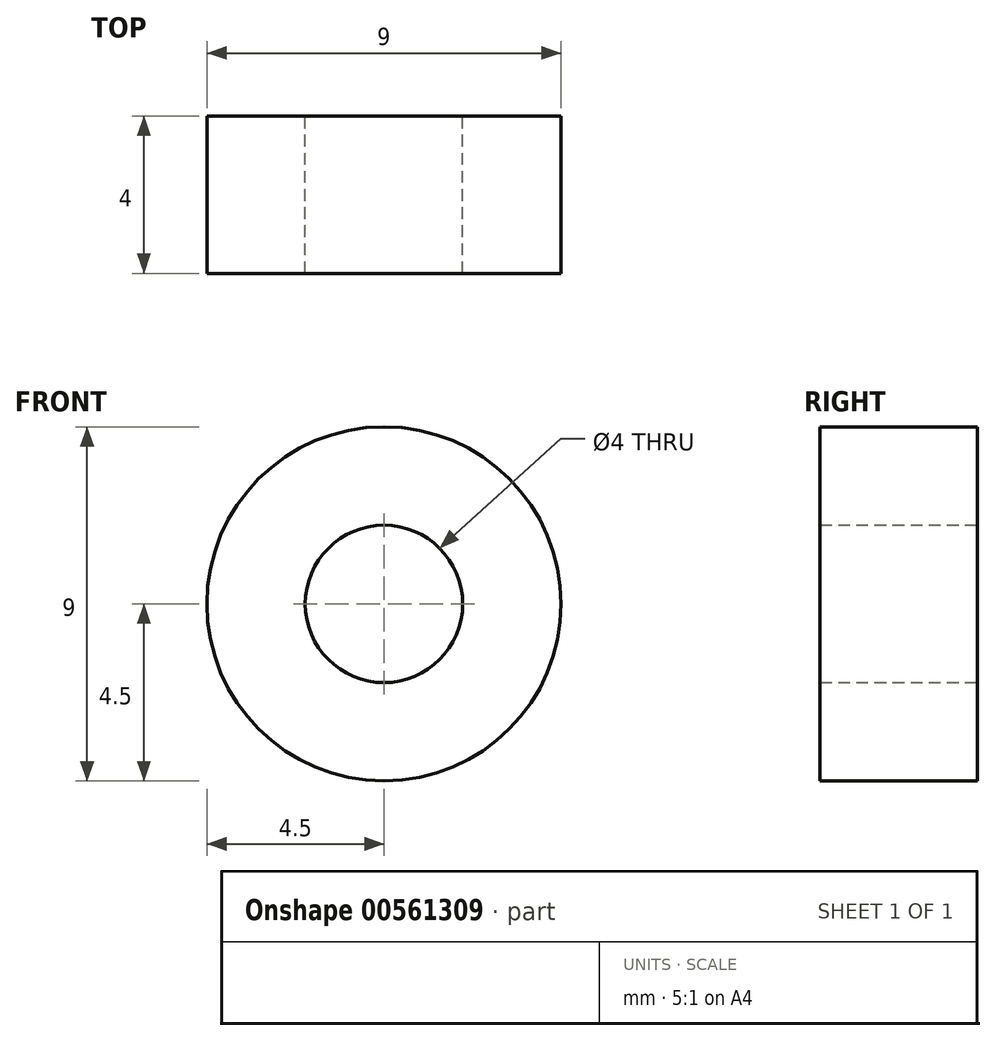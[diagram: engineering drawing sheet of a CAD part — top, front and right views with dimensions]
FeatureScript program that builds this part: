
annotation { "Feature Type Name" : "Feature", "Feature Type Description" : "" }
export const myFeature = defineFeature(function(context is Context, id is Id, definition is map)
    precondition{}
    {
        {
            var Q0;
            Q0=qCreatedBy(makeId("Front.planeOp"),FACE);
            var sketch = newSketch(context, id + "F0", { "sketchPlane" : qUnion([Q0])});
            skCircle(sketch, "E0", {"center": v(0, 0) * mm, "radius": 4.5 * mm});
            skCircle(sketch, "E1", {"center": v(0, 0) * mm, "radius": 2 * mm});
            skSolve(sketch);
        }
        {
            var Q0;
            Q0 = qSketchRegion(id + "F0", true);
            extrude(context, id + "F1", {"entities" : qUnion([Q0]), "depth" : 4 * mm, "offsetDistance" : 25 * mm});
        }
    });
